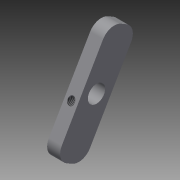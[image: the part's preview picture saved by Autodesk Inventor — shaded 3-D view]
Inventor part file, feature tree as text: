
AUTODESK INVENTOR PART (.ipt)
format: ipt  version: 2015 (Build 190159000, 159)  size: 123,392 bytes
history: native  units: mm
features: hole x3, sketch x3, extrude x1, fillet x1, projected_geometry x1
ambient origin geometry x8: Origin, YZ Plane, XZ Plane, XY Plane, X Axis, Y Axis, Z Axis, Center Point
bodies: Solid1 (feature_tree)
feature tree (9):
  extrude  "Extrusion1"  Depth=50.0mm
  hole  "Hole1"  [1 undecoded]
  hole  "Hole2"  [1 undecoded]
  hole  "Hole3"  [1 undecoded]
  fillet  "Fillet1"  Radius=6.0mm
  sketch  "Sketch2"  dims[d1=15.0mm d2=50.0mm]
  sketch  "Sketch3"  dims[d4=60.0deg d5=6.0mm d6=0.0mm]
  sketch  "Sketch4"  dims[d7=8.0mm d8=6.0mm d9=4.0mm d10=2.0mm d11=90.0deg d12=8.0mm d13=20.594885mm d14=3.242mm d15=8.0mm d16=4.0mm d17=2.0mm d18=90.0deg d19=11.8mm d20=20.594885mm d21=20.0mm d22=20.0mm d23=3.459mm d24=8.0mm d25=4.0mm d26=2.0mm d27=90.0deg d28=4.0mm d29=20.594885mm d30=6.0mm d31=1.0mm d32=1.0mm]
  projected_geometry  "Projected Loop1"
note: 3 required parameter values undecoded (feature->parameter linkage not recoverable at this tier; creation-order binding heuristic only, values carry confidence <= 0.55)
